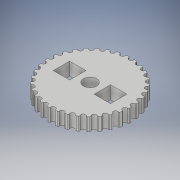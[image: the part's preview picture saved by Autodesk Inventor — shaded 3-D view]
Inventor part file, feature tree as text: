
AUTODESK INVENTOR PART (.ipt)
format: ipt  version: 2019 (Build 230136000, 136)  size: 305,152 bytes
history: native  units: mm
features: sketch x3, extrude x2, other x1, pattern_circular x1, hole x1
ambient origin geometry x8: Origin, YZ Plane, XZ Plane, XY Plane, X Axis, Y Axis, Z Axis, Center Point
bodies: Body1 (feature_tree)
feature tree (8):
  other  "ソリッド1"
  extrude  "押し出し1"  Depth=52.52mm
  pattern_circular  "円形状パターン1"  [2 undecoded]
  extrude  "押し出し2"  Depth=44.0mm
  hole  "穴1"  [1 undecoded]
  sketch  "スケッチ1"
  sketch  "スケッチ2"
  sketch  "スケッチ3"
note: 3 required parameter values undecoded (feature->parameter linkage not recoverable at this tier; creation-order binding heuristic only, values carry confidence <= 0.55)
